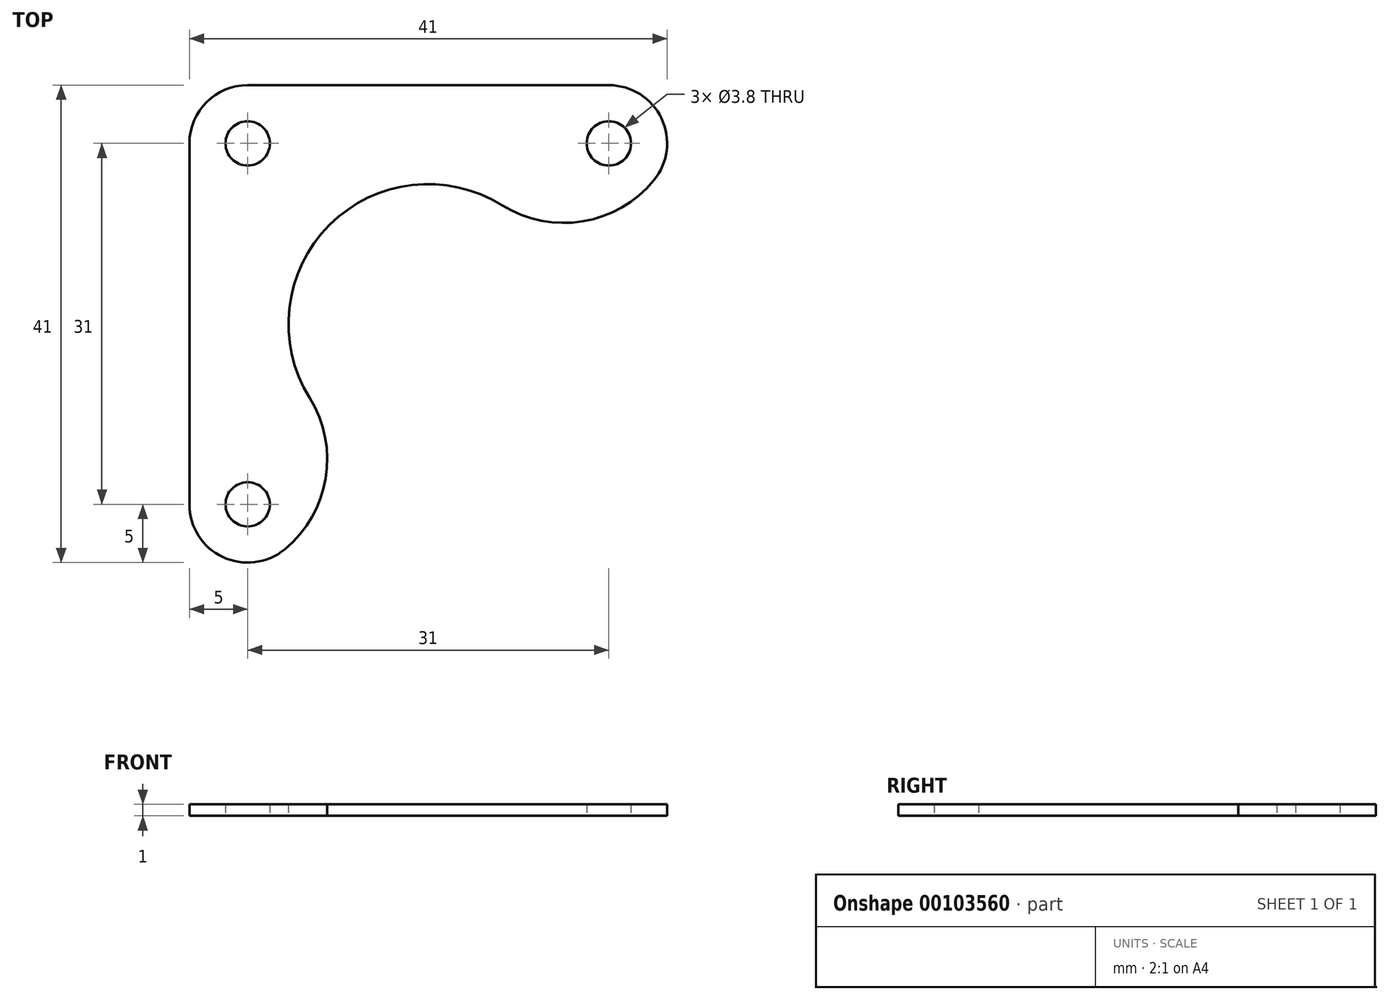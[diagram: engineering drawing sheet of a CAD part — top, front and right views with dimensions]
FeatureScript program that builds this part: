
annotation { "Feature Type Name" : "Feature", "Feature Type Description" : "" }
export const myFeature = defineFeature(function(context is Context, id is Id, definition is map)
    precondition{}
    {
        {
            var Q0;
            Q0=qCreatedBy(makeId("Top.planeOp"),FACE);
            var sketch = newSketch(context, id + "F0", { "sketchPlane" : qUnion([Q0])});
            skLineSegment(sketch, "E0.bottom", {"start": v(15.5, -15.5) * mm, "end": v(-15.5, -15.5) * mm, "construction": true});
            skLineSegment(sketch, "E0.top", {"start": v(15.5, 15.5) * mm, "end": v(-15.5, 15.5) * mm, "construction": true});
            skLineSegment(sketch, "E0.left", {"start": v(15.5, -15.5) * mm, "end": v(15.5, 15.5) * mm, "construction": true});
            skLineSegment(sketch, "E0.right", {"start": v(-15.5, -15.5) * mm, "end": v(-15.5, 15.5) * mm, "construction": true});
            skPoint(sketch, "E0.middle", {"position": v(0, 0) * mm});
            skCircle(sketch, "E1", {"center": v(-15.5, 15.5) * mm, "radius": 1.9 * mm});
            skCircle(sketch, "E2", {"center": v(15.5, 15.5) * mm, "radius": 1.9 * mm});
            skCircle(sketch, "E3", {"center": v(-15.5, -15.5) * mm, "radius": 1.9 * mm});
            skLineSegment(sketch, "E4.bottom", {"start": v(-21, 21) * mm, "end": v(21, 21) * mm, "construction": true});
            skLineSegment(sketch, "E4.top", {"start": v(-21, -21) * mm, "end": v(21, -21) * mm, "construction": true});
            skLineSegment(sketch, "E4.left", {"start": v(-21, 21) * mm, "end": v(-21, -21) * mm, "construction": true});
            skLineSegment(sketch, "E4.right", {"start": v(21, 21) * mm, "end": v(21, -21) * mm, "construction": true});
            skCircle(sketch, "E5", {"center": v(15.5, 15.5) * mm, "radius": 5 * mm});
            skCircle(sketch, "E6", {"center": v(-15.5, 15.5) * mm, "radius": 5 * mm});
            skCircle(sketch, "E7", {"center": v(-15.5, -15.5) * mm, "radius": 5 * mm});
            skLineSegment(sketch, "E8", {"start": v(-15.5, 20.5) * mm, "end": v(15.5, 20.5) * mm});
            skLineSegment(sketch, "E9", {"start": v(-20.5, 15.5) * mm, "end": v(-20.5, -15.5) * mm});
            skArc(sketch, "E10", {"start": v(-10.18, -6.35) * mm, "mid": v(-8.49, 8.49) * mm, "end": v(6.35, 10.18) * mm});
            skArc(sketch, "E11", {"start": v(6.35, 10.18) * mm, "mid": v(13.26, 8.8) * mm, "end": v(19.37, 12.33) * mm});
            skArc(sketch, "E12", {"start": v(-12.33, -19.37) * mm, "mid": v(-8.8, -13.26) * mm, "end": v(-10.18, -6.35) * mm});
            skSolve(sketch);
        }
        {
            var Q0;
            Q0=makeQuery(id+"F0.imprint","IMPRINT",FACE,{"disambiguationData":[TD([[makeQuery(id+"F0.imprint","IMPRINT",EDGE,{"derivedFrom":sQuery(id+"F0.wireOp",EDGE,"E1")}),-1.0]])]});
            var Q1;
            {var subQ0=sQuery(id+"F0.wireOp",EDGE,"E8");Q1=makeQuery(id+"F0.imprint","IMPRINT",FACE,{"disambiguationData":[TD([[makeQuery(id+"F0.imprint","IMPRINT",EDGE,{"derivedFrom":subQ0}),-1.0]])]});}
            var Q2;
            Q2=makeQuery(id+"F0.imprint","IMPRINT",FACE,{"disambiguationData":[TD([[makeQuery(id+"F0.imprint","IMPRINT",EDGE,{"derivedFrom":sQuery(id+"F0.wireOp",EDGE,"E2")}),-1.0]])]});
            var Q3;
            Q3=makeQuery(id+"F0.imprint","IMPRINT",FACE,{"disambiguationData":[TD([[makeQuery(id+"F0.imprint","IMPRINT",EDGE,{"derivedFrom":sQuery(id+"F0.wireOp",EDGE,"E3")}),-1.0]])]});
            extrude(context, id + "F1", {"entities" : qUnion([Q0, Q1, Q2, Q3]), "depth" : 1 * mm});
        }
    });
